# Revit family: Plumbing-Water-Closet-Sloan-Valve-ST-2459
name_source: partatom
category: Plumbing Fixtures
units: mm (PartAtom-declared; Revit-internal decimal feet)

## family parameters
Cut with Voids When Loaded = No
Host = Face
OmniClass Number = 23.45.05.21.11.11
OmniClass Title = Water Operated Water Closets
Part Type = Normal
Room Calculation Point = No
Round Connector Dimension = Use Diameter
Shared = No

## types (5) — shared parameters
Assembly Code = D2010
CW Connection = Yes
CWFU = 10
Depth = 26.75 "
Edition number = 1
Flush Rate = 1.1 – 1.6 gpf (4.2 – 6.0 Lpf) - Flush volume determined by the flushometer used with the fixture
HW Connection = No
Height = 13.25 "
Keynote = 15410
Manufacturer = Sloan Valve
Maximum Static Pressure = 80 PSI (552 kPa)
Minimum Flowing Pressure = 25 PSI (172 kPa)
Product data url = https://www.bimobject.com
Sanitary Drain Connection Diameter = 2"
URL = www.sloanvalve.com
Valve Pressure Drop = 0.00 psi
Vent Connection = No
WFU = 10
Waste Connection = Yes
Water Inlet Connection Diameter = 2"
Width = 15 "
zero-valued in all types: Default Elevation, HWFU

## per-type parameters (varying)
| type | Description | Part Number | Product Material | z_Bed Pan Lugs |
| ST-2459 | Vitreous China Wall-Mounted Water Closet | 2102459 | Sloan Valve - Vitreous China - White | No |
| ST-2459-BPL | Bed Pan Lugs, Vitreous China Wall-Mounted Water Closet | 2112459 | Sloan Valve - Vitreous China - White | Yes |
| ST-2459-BPL-STG | Bed Pan Lugs, , Vitreous China Wall-Mounted Water Closet with SloanTec® Glaze | 2172450 | Sloan Valve - Vitreous China - SloanTec Glaze White | Yes |
| ST-2459-CO | Carbon Offset, Vitreous China Wall-Mounted Water Closet. | 2102459T | Sloan Valve - Vitreous China - White | No |
| ST-2459-STG | Vitreous China Wall-Mounted Water Closet with SloanTec® Glaze. | 2172459 | Sloan Valve - Vitreous China - SloanTec Glaze White | No |

note: column(s) folded — value = type name in every type: Model

## geometry (parser evidence)
native form markers: Sweep x6
no freeform markers — native parametric forms only
